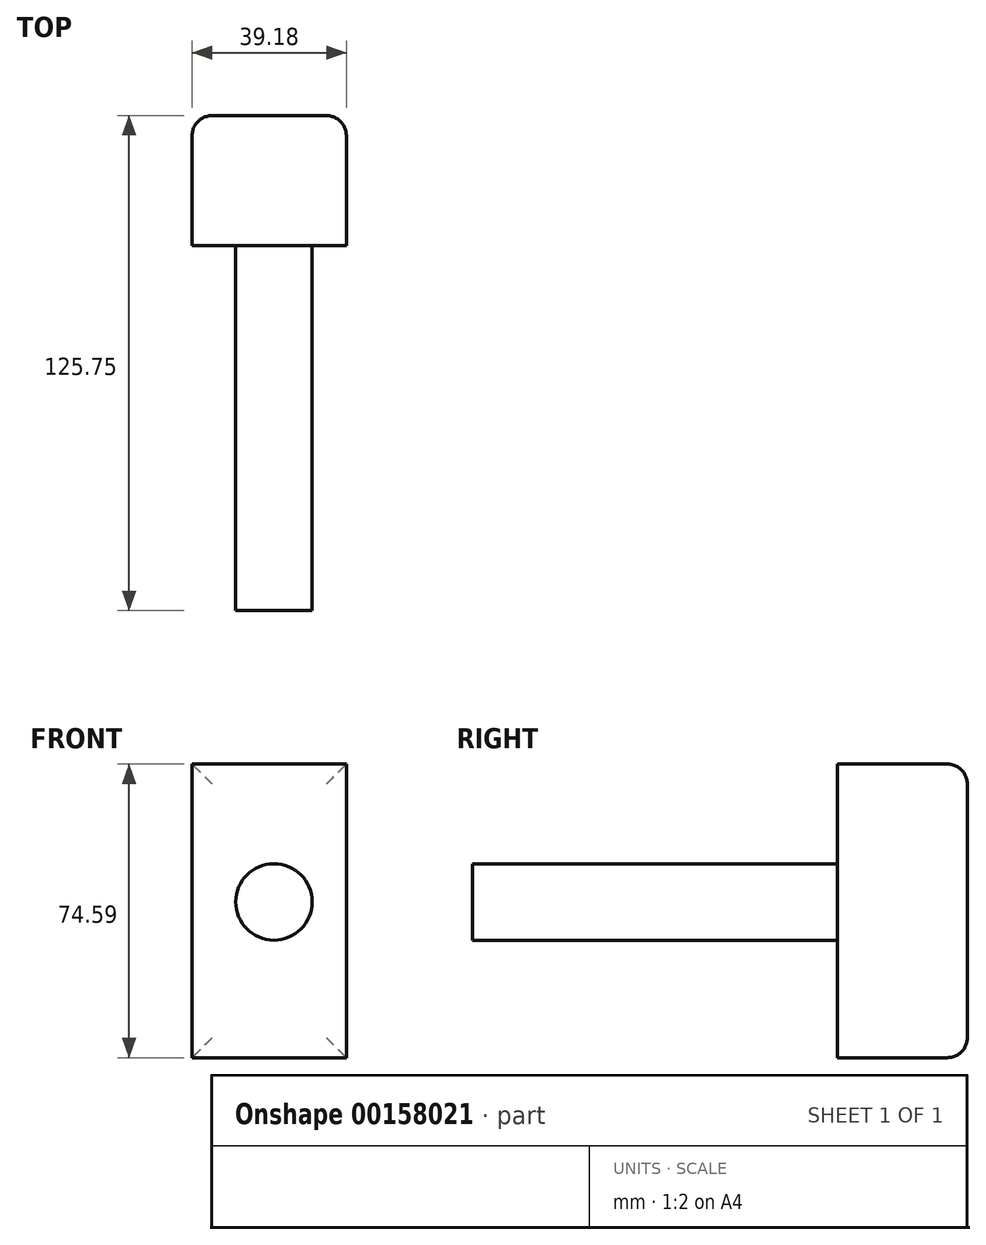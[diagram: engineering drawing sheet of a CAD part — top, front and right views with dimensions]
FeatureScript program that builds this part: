
annotation { "Feature Type Name" : "Feature", "Feature Type Description" : "" }
export const myFeature = defineFeature(function(context is Context, id is Id, definition is map)
    precondition{}
    {
        {
            var Q0;
            Q0=qCreatedBy(makeId("Front.planeOp"),FACE);
            var sketch = newSketch(context, id + "F0", { "sketchPlane" : qUnion([Q0])});
            skLineSegment(sketch, "E0.bottom", {"start": v(0, 0) * mm, "end": v(39.18, 0) * mm});
            skLineSegment(sketch, "E0.top", {"start": v(0, 74.6) * mm, "end": v(39.18, 74.6) * mm});
            skLineSegment(sketch, "E0.left", {"start": v(0, 0) * mm, "end": v(0, 74.6) * mm});
            skLineSegment(sketch, "E0.right", {"start": v(39.18, 0) * mm, "end": v(39.18, 74.6) * mm});
            skSolve(sketch);
        }
        {
            var Q0;
            Q0=makeQuery(id+"F0.imprint","IMPRINT",FACE,{"disambiguationData":[TD([[makeQuery(id+"F0.imprint","IMPRINT",EDGE,{"derivedFrom":sQuery(id+"F0.wireOp",EDGE,"E0.bottom")}),1.0]])]});
            extrude(context, id + "F1", {"entities" : qUnion([Q0]), "depth" : 33 * mm});
        }
        {
            var Q0;
            Q0=makeQuery(id+"F1.opExtrude","CAP_FACE",FACE,{"disambiguationData":[OSD([sQuery(id+"F0.wireOp",EDGE,"E0.bottom"),sQuery(id+"F0.wireOp",EDGE,"E0.top"),sQuery(id+"F0.wireOp",EDGE,"E0.left"),sQuery(id+"F0.wireOp",EDGE,"E0.right")])],"isStart":false});
            var sketch = newSketch(context, id + "F2", { "sketchPlane" : qUnion([Q0])});
            skCircle(sketch, "E1", {"center": v(20.78, 39.57) * mm, "radius": 9.71 * mm});
            skSolve(sketch);
        }
        {
            var Q0;
            Q0=makeQuery(id+"F2.imprint","IMPRINT",FACE,{"disambiguationData":[TD([[makeQuery(id+"F2.imprint","IMPRINT",EDGE,{"derivedFrom":sQuery(id+"F2.wireOp",EDGE,"E1")}),1.0]])]});
            extrude(context, id + "F3", {"entities" : qUnion([Q0]), "operationType" : NewBodyOperationType.ADD, "depth" : 92.75 * mm});
        }
        {
            var Q0;
            Q0=makeQuery(id+"F1.opExtrude","CAP_EDGE",EDGE,{"disambiguationData":[OSD([sQuery(id+"F0.wireOp",EDGE,"E0.right")])],"isStart":true});
            var Q1;
            Q1=makeQuery(id+"F1.opExtrude","CAP_EDGE",EDGE,{"disambiguationData":[OSD([sQuery(id+"F0.wireOp",EDGE,"E0.top")])],"isStart":true});
            var Q2;
            Q2=makeQuery(id+"F1.opExtrude","CAP_EDGE",EDGE,{"disambiguationData":[OSD([sQuery(id+"F0.wireOp",EDGE,"E0.left")])],"isStart":true});
            var Q3;
            Q3=makeQuery(id+"F1.opExtrude","CAP_EDGE",EDGE,{"disambiguationData":[OSD([sQuery(id+"F0.wireOp",EDGE,"E0.bottom")])],"isStart":true});
            fillet(context, id + "F4", {"entities" : qUnion([Q0, Q1, Q2, Q3]), "radius" : 5 * mm, "tangentPropagation" : true, "allowEdgeOverflow" : false});
        }
    });
